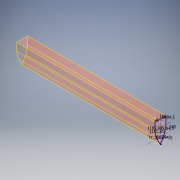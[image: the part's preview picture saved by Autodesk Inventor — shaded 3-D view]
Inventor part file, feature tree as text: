
AUTODESK INVENTOR PART (.ipt)
format: ipt  version: 2018 (Build 220112000, 112)  size: 114,176 bytes
history: native  units: mm
features: sketch x2, other x1, sweep x1
ambient origin geometry x8: Origin, YZ Plane, XZ Plane, XY Plane, X Axis, Y Axis, Z Axis, Center Point
bodies: Body1 (feature_tree)
feature tree (4):
  sketch  "Sketch2"  dims[d1=240.0mm d4=0.0mm d5=0.0mm]
  sketch  "Sketch3"  dims[d10=26.495542mm d11=28.955734mm d12=28.955734mm d15=120.0mm d16=84.5mm d18=84.5mm d19=83.443035mm d20=1500.0mm]
  other  "Srf1"
  sweep  "SweepSrf1"
